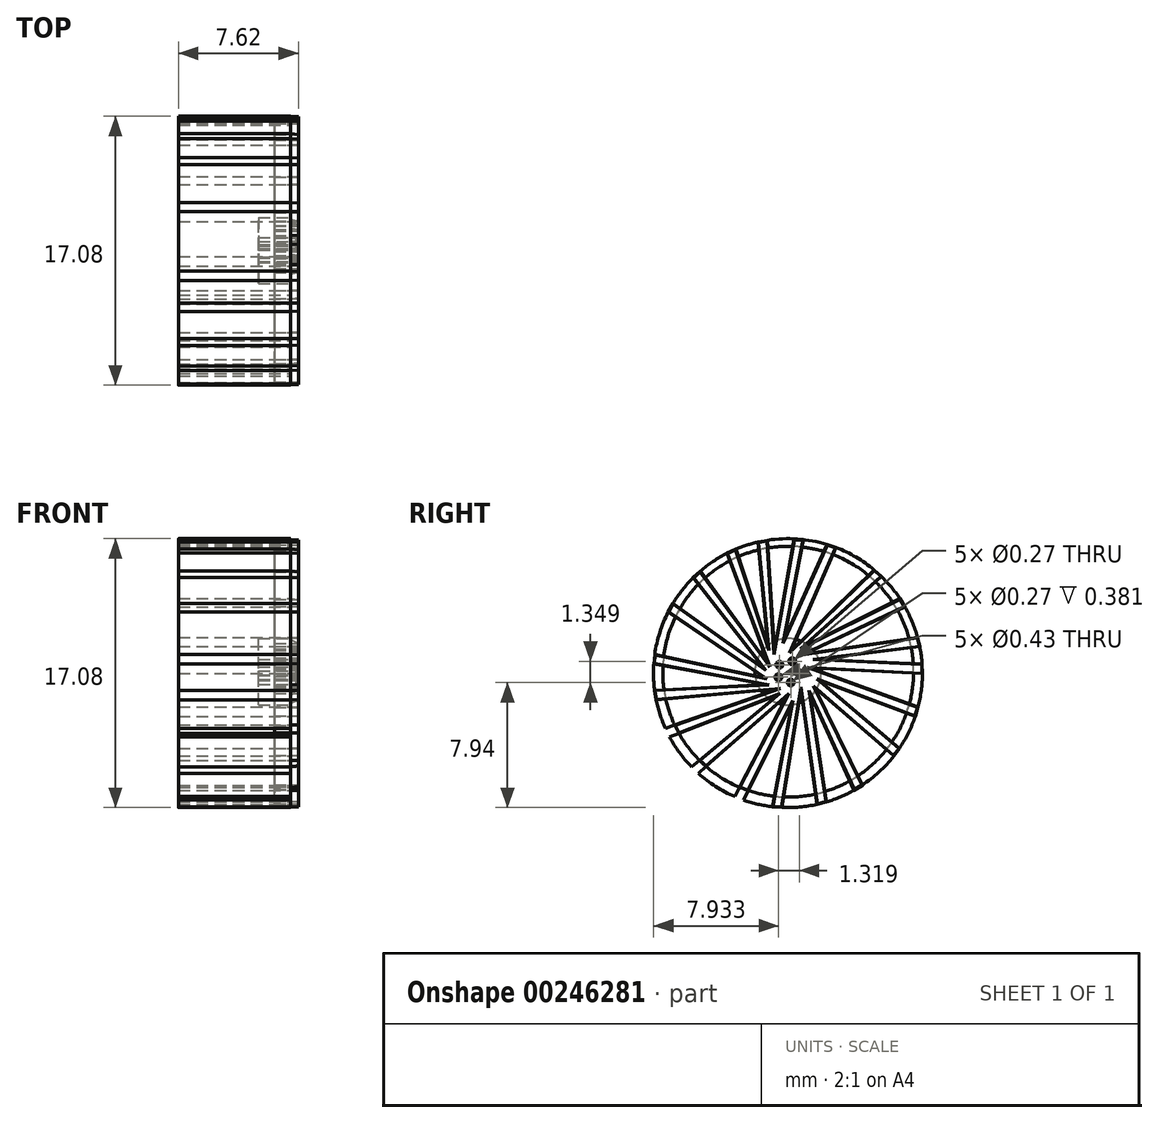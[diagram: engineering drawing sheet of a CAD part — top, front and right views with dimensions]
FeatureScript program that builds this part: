
annotation { "Feature Type Name" : "Feature", "Feature Type Description" : "" }
export const myFeature = defineFeature(function(context is Context, id is Id, definition is map)
    precondition{}
    {
        {
            var Q0;
            Q0=qCreatedBy(makeId("Right.planeOp"),FACE);
            var sketch = newSketch(context, id + "F0", { "sketchPlane" : qUnion([Q0])});
            skCircle(sketch, "E0", {"center": v(-0.01, -0.1) * mm, "radius": 8.54 * mm});
            skCircle(sketch, "E1", {"center": v(0, 0) * mm, "radius": 2.1 * mm});
            skCircle(sketch, "E2", {"center": v(0, 0) * mm, "radius": 7.96 * mm});
            skLineSegment(sketch, "E3", {"start": v(-0.39, -8.62) * mm, "end": v(0.81, -1.16) * mm});
            skLineSegment(sketch, "E4", {"start": v(0.81, -1.16) * mm, "end": v(1.84, -8.43) * mm});
            skLineSegment(sketch, "E5", {"start": v(2.43, -8.27) * mm, "end": v(1.38, -1.38) * mm});
            skLineSegment(sketch, "E6", {"start": v(1.38, -1.38) * mm, "end": v(4.19, -7.53) * mm});
            skLineSegment(sketch, "E7", {"start": v(-1, -8.58) * mm, "end": v(0.24, -2) * mm});
            skLineSegment(sketch, "E8", {"start": v(0.24, -2) * mm, "end": v(-2.83, -8.16) * mm});
            skLineSegment(sketch, "E9", {"start": v(-2.83, -8.16) * mm, "end": v(-3.4, -7.93) * mm});
            skLineSegment(sketch, "E10", {"start": v(-3.4, -7.93) * mm, "end": v(-0.05, -1.48) * mm});
            skLineSegment(sketch, "E11", {"start": v(-0.05, -1.48) * mm, "end": v(-5.7, -6.46) * mm});
            skLineSegment(sketch, "E12", {"start": v(-5.7, -6.46) * mm, "end": v(-6.14, -6.04) * mm});
            skLineSegment(sketch, "E13", {"start": v(-6.14, -6.04) * mm, "end": v(-0.66, -1.47) * mm});
            skLineSegment(sketch, "E14", {"start": v(-0.66, -1.47) * mm, "end": v(-7.53, -4.14) * mm});
            skLineSegment(sketch, "E15", {"start": v(-7.53, -4.14) * mm, "end": v(-7.8, -3.6) * mm});
            skLineSegment(sketch, "E16", {"start": v(-7.8, -3.6) * mm, "end": v(-0.7, -1.1) * mm});
            skLineSegment(sketch, "E17", {"start": v(-0.7, -1.1) * mm, "end": v(-8.39, -1.78) * mm});
            skLineSegment(sketch, "E18", {"start": v(-8.48, -1.18) * mm, "end": v(-1.45, -0.82) * mm});
            skLineSegment(sketch, "E19", {"start": v(-1.45, -0.82) * mm, "end": v(-8.53, 0.5) * mm});
            skLineSegment(sketch, "E20", {"start": v(-8.47, 1.1) * mm, "end": v(-1.46, -0.4) * mm});
            skLineSegment(sketch, "E21", {"start": v(-1.46, -0.4) * mm, "end": v(-7.62, 3.8) * mm});
            skLineSegment(sketch, "E22", {"start": v(-7.32, 4.33) * mm, "end": v(-1.54, 0.2) * mm});
            skLineSegment(sketch, "E23", {"start": v(-1.54, 0.2) * mm, "end": v(-6.03, 5.97) * mm});
            skLineSegment(sketch, "E24", {"start": v(-5.58, 6.38) * mm, "end": v(-1.25, 0.47) * mm});
            skLineSegment(sketch, "E25", {"start": v(4.7, -7.2) * mm, "end": v(1.68, -1) * mm});
            skLineSegment(sketch, "E26", {"start": v(1.68, -1) * mm, "end": v(6.7, -5.36) * mm});
            skLineSegment(sketch, "E27", {"start": v(7.06, -4.87) * mm, "end": v(1.98, -0.54) * mm});
            skLineSegment(sketch, "E28", {"start": v(1.98, -0.54) * mm, "end": v(8.07, -2.83) * mm});
            skLineSegment(sketch, "E29", {"start": v(8.5, 0.48) * mm, "end": v(1.87, 0.78) * mm});
            skLineSegment(sketch, "E30", {"start": v(1.87, 0.78) * mm, "end": v(8.36, 1.6) * mm});
            skLineSegment(sketch, "E31", {"start": v(8.22, 2.19) * mm, "end": v(1.05, 1.12) * mm});
            skLineSegment(sketch, "E32", {"start": v(1.05, 1.12) * mm, "end": v(7.42, 4.12) * mm});
            skLineSegment(sketch, "E33", {"start": v(7.1, 4.64) * mm, "end": v(0.95, 1.57) * mm});
            skLineSegment(sketch, "E34", {"start": v(0.95, 1.57) * mm, "end": v(5.92, 6.05) * mm});
            skLineSegment(sketch, "E35", {"start": v(5.46, 6.46) * mm, "end": v(0.17, 1.3) * mm});
            skLineSegment(sketch, "E36", {"start": v(0.17, 1.3) * mm, "end": v(3.04, 7.88) * mm});
            skLineSegment(sketch, "E37", {"start": v(2.47, 8.08) * mm, "end": v(-0.26, 2.01) * mm});
            skLineSegment(sketch, "E38", {"start": v(-0.26, 2.01) * mm, "end": v(0.99, 8.39) * mm});
            skLineSegment(sketch, "E39", {"start": v(0.38, 8.39) * mm, "end": v(-0.88, 1.31) * mm});
            skLineSegment(sketch, "E40", {"start": v(-0.88, 1.31) * mm, "end": v(-1.3, 8.35) * mm});
            skLineSegment(sketch, "E41", {"start": v(-1.9, 8.24) * mm, "end": v(-1.28, 1.57) * mm});
            skLineSegment(sketch, "E42", {"start": v(-1.28, 1.57) * mm, "end": v(-3.32, 7.78) * mm});
            skLineSegment(sketch, "E43", {"start": v(-3.87, 7.53) * mm, "end": v(-1.25, 0.47) * mm});
            skLineSegment(sketch, "E44", {"start": v(-1.9, 8.24) * mm, "end": v(-1.3, 8.35) * mm});
            skLineSegment(sketch, "E45", {"start": v(0.38, 8.39) * mm, "end": v(0.99, 8.39) * mm});
            skLineSegment(sketch, "E46", {"start": v(2.47, 8.08) * mm, "end": v(3.04, 7.88) * mm});
            skLineSegment(sketch, "E47", {"start": v(-3.32, 7.78) * mm, "end": v(-3.87, 7.53) * mm});
            skLineSegment(sketch, "E48", {"start": v(-5.58, 6.38) * mm, "end": v(-6.03, 5.97) * mm});
            skLineSegment(sketch, "E49", {"start": v(-7.32, 4.33) * mm, "end": v(-7.62, 3.8) * mm});
            skLineSegment(sketch, "E50", {"start": v(-7.8, -3.6) * mm, "end": v(-7.53, -4.14) * mm});
            skLineSegment(sketch, "E51", {"start": v(-6.14, -6.04) * mm, "end": v(-5.7, -6.46) * mm});
            skLineSegment(sketch, "E52", {"start": v(-3.4, -7.93) * mm, "end": v(-2.83, -8.16) * mm});
            skLineSegment(sketch, "E53", {"start": v(-1, -8.58) * mm, "end": v(-0.39, -8.62) * mm});
            skLineSegment(sketch, "E54", {"start": v(1.84, -8.43) * mm, "end": v(2.43, -8.27) * mm});
            skLineSegment(sketch, "E55", {"start": v(4.19, -7.53) * mm, "end": v(4.7, -7.2) * mm});
            skLineSegment(sketch, "E56", {"start": v(6.7, -5.36) * mm, "end": v(7.06, -4.87) * mm});
            skLineSegment(sketch, "E57", {"start": v(8.53, -0.13) * mm, "end": v(8.5, 0.48) * mm});
            skLineSegment(sketch, "E58", {"start": v(8.36, 1.6) * mm, "end": v(8.22, 2.19) * mm});
            skLineSegment(sketch, "E59", {"start": v(7.1, 4.64) * mm, "end": v(7.42, 4.12) * mm});
            skLineSegment(sketch, "E60", {"start": v(5.46, 6.46) * mm, "end": v(5.92, 6.05) * mm});
            skLineSegment(sketch, "E61", {"start": v(-8.47, 1.1) * mm, "end": v(-8.53, 0.5) * mm});
            skLineSegment(sketch, "E62", {"start": v(-8.39, -1.78) * mm, "end": v(-8.48, -1.18) * mm});
            skLineSegment(sketch, "E63", {"start": v(1.4, 0.23) * mm, "end": v(8.25, -2.25) * mm});
            skLineSegment(sketch, "E64", {"start": v(1.4, 0.23) * mm, "end": v(8.53, -0.13) * mm});
            skLineSegment(sketch, "E65", {"start": v(8.25, -2.25) * mm, "end": v(8.07, -2.83) * mm});
            skCircle(sketch, "E66", {"center": v(0, 0) * mm, "radius": 0.52 * mm});
            skCircle(sketch, "E67", {"center": v(0.26, 0.66) * mm, "radius": 0.19 * mm});
            skCircle(sketch, "E68", {"center": v(-0.55, 0.44) * mm, "radius": 0.19 * mm});
            skCircle(sketch, "E69", {"center": v(0.7, -0.1) * mm, "radius": 0.19 * mm});
            skCircle(sketch, "E70", {"center": v(-0.62, -0.35) * mm, "radius": 0.19 * mm});
            skCircle(sketch, "E71", {"center": v(0.16, -0.69) * mm, "radius": 0.19 * mm});
            skCircle(sketch, "E72", {"center": v(0.26, 0.66) * mm, "radius": 0.13 * mm});
            skCircle(sketch, "E73", {"center": v(-0.55, 0.44) * mm, "radius": 0.13 * mm});
            skCircle(sketch, "E74", {"center": v(-0.62, -0.35) * mm, "radius": 0.13 * mm});
            skCircle(sketch, "E75", {"center": v(0.16, -0.69) * mm, "radius": 0.13 * mm});
            skCircle(sketch, "E76", {"center": v(0.7, -0.1) * mm, "radius": 0.13 * mm});
            skLineSegment(sketch, "E77", {"start": v(-2, -1.56) * mm, "end": v(-1.87, -1.94) * mm});
            skLineSegment(sketch, "E78", {"start": v(-1.64, -2.3) * mm, "end": v(-1.36, -2.64) * mm});
            skLineSegment(sketch, "E79", {"start": v(-0.76, -2.86) * mm, "end": v(-0.3, -3.1) * mm});
            skLineSegment(sketch, "E80", {"start": v(0.04, -3.1) * mm, "end": v(0.49, -3.18) * mm});
            skLineSegment(sketch, "E81", {"start": v(1.1, -3.26) * mm, "end": v(1.66, -3.18) * mm});
            skLineSegment(sketch, "E82", {"start": v(2.12, -2.99) * mm, "end": v(2.55, -2.78) * mm});
            skLineSegment(sketch, "E83", {"start": v(3.07, -2.21) * mm, "end": v(3.44, -1.78) * mm});
            skLineSegment(sketch, "E84", {"start": v(3.64, -1.17) * mm, "end": v(3.74, -0.61) * mm});
            skLineSegment(sketch, "E85", {"start": v(-2.23, -1.23) * mm, "end": v(-2.25, -0.86) * mm});
            skLineSegment(sketch, "E86", {"start": v(-2.49, -0.62) * mm, "end": v(-2.4, -0.2) * mm});
            skLineSegment(sketch, "E87", {"start": v(-2.6, 0.38) * mm, "end": v(-2.33, 0.76) * mm});
            skLineSegment(sketch, "E88", {"start": v(-2.26, 1.12) * mm, "end": v(-1.91, 1.37) * mm});
            skLineSegment(sketch, "E89", {"start": v(-1.76, 1.84) * mm, "end": v(-1.4, 1.96) * mm});
            skSolve(sketch);
        }
        {
            var Q0;
            {var subQ36=sQuery(id+"F0.wireOp",EDGE,"E67");Q0=makeQuery(id+"F0.imprint","IMPRINT",FACE,{"disambiguationData":[TD([[makeQuery(id+"F0.imprint","IMPRINT",EDGE,{"derivedFrom":subQ36}),-1.0]])]});}
            var Q1;
            {var subQ0=sQuery(id+"F0.wireOp",EDGE,"E32");var subQ1=sQuery(id+"F0.wireOp",EDGE,"E1");var subQ2=makeQuery(id+"F0.imprint","INTERSECT",VERTEX,{"derivedFrom":[subQ1,subQ0]});Q1=makeQuery(id+"F0.imprint","IMPRINT",FACE,{"disambiguationData":[TD([[makeQuery(id+"F0.imprint","IMPRINT",EDGE,{"disambiguationData":[TD([[subQ2,-1.0]])],"derivedFrom":subQ1}),-1.0]])]});}
            var Q2;
            {var subQ0=sQuery(id+"F0.wireOp",EDGE,"E34");var subQ1=sQuery(id+"F0.wireOp",EDGE,"E1");var subQ2=makeQuery(id+"F0.imprint","INTERSECT",VERTEX,{"derivedFrom":[subQ1,subQ0]});Q2=makeQuery(id+"F0.imprint","IMPRINT",FACE,{"disambiguationData":[TD([[makeQuery(id+"F0.imprint","IMPRINT",EDGE,{"disambiguationData":[TD([[subQ2,-1.0]])],"derivedFrom":subQ1}),-1.0]])]});}
            var Q3;
            {var subQ0=sQuery(id+"F0.wireOp",EDGE,"E36");var subQ1=sQuery(id+"F0.wireOp",EDGE,"E1");var subQ2=makeQuery(id+"F0.imprint","INTERSECT",VERTEX,{"derivedFrom":[subQ1,subQ0]});Q3=makeQuery(id+"F0.imprint","IMPRINT",FACE,{"disambiguationData":[TD([[makeQuery(id+"F0.imprint","IMPRINT",EDGE,{"disambiguationData":[TD([[subQ2,-1.0]])],"derivedFrom":subQ1}),-1.0]])]});}
            var Q4;
            {var subQ0=sQuery(id+"F0.wireOp",EDGE,"E38");var subQ1=sQuery(id+"F0.wireOp",EDGE,"E1");var subQ2=makeQuery(id+"F0.imprint","INTERSECT",VERTEX,{"derivedFrom":[subQ1,subQ0]});Q4=makeQuery(id+"F0.imprint","IMPRINT",FACE,{"disambiguationData":[TD([[makeQuery(id+"F0.imprint","IMPRINT",EDGE,{"disambiguationData":[TD([[subQ2,-1.0]])],"derivedFrom":subQ1}),-1.0]])]});}
            var Q5;
            {var subQ0=sQuery(id+"F0.wireOp",EDGE,"E30");var subQ1=sQuery(id+"F0.wireOp",EDGE,"E1");var subQ2=makeQuery(id+"F0.imprint","INTERSECT",VERTEX,{"derivedFrom":[subQ1,subQ0]});Q5=makeQuery(id+"F0.imprint","IMPRINT",FACE,{"disambiguationData":[TD([[makeQuery(id+"F0.imprint","IMPRINT",EDGE,{"disambiguationData":[TD([[subQ2,-1.0]])],"derivedFrom":subQ1}),-1.0]])]});}
            var Q6;
            {var subQ0=sQuery(id+"F0.wireOp",EDGE,"E29");var subQ1=sQuery(id+"F0.wireOp",EDGE,"E1");var subQ2=makeQuery(id+"F0.imprint","INTERSECT",VERTEX,{"derivedFrom":[subQ1,subQ0]});Q6=makeQuery(id+"F0.imprint","IMPRINT",FACE,{"disambiguationData":[TD([[makeQuery(id+"F0.imprint","IMPRINT",EDGE,{"disambiguationData":[TD([[subQ2,1.0]])],"derivedFrom":subQ1}),-1.0]])]});}
            var Q7;
            {var subQ0=sQuery(id+"F0.wireOp",EDGE,"E28");var subQ1=sQuery(id+"F0.wireOp",EDGE,"E1");var subQ2=makeQuery(id+"F0.imprint","INTERSECT",VERTEX,{"derivedFrom":[subQ1,subQ0]});Q7=makeQuery(id+"F0.imprint","IMPRINT",FACE,{"disambiguationData":[TD([[makeQuery(id+"F0.imprint","IMPRINT",EDGE,{"disambiguationData":[TD([[subQ2,-1.0]])],"derivedFrom":subQ1}),-1.0]])]});}
            var Q8;
            {var subQ0=sQuery(id+"F0.wireOp",EDGE,"E26");var subQ1=sQuery(id+"F0.wireOp",EDGE,"E1");var subQ2=makeQuery(id+"F0.imprint","INTERSECT",VERTEX,{"derivedFrom":[subQ1,subQ0]});Q8=makeQuery(id+"F0.imprint","IMPRINT",FACE,{"disambiguationData":[TD([[makeQuery(id+"F0.imprint","IMPRINT",EDGE,{"disambiguationData":[TD([[subQ2,-1.0]])],"derivedFrom":subQ1}),-1.0]])]});}
            var Q9;
            {var subQ0=sQuery(id+"F0.wireOp",EDGE,"E6");var subQ1=sQuery(id+"F0.wireOp",EDGE,"E1");var subQ2=makeQuery(id+"F0.imprint","INTERSECT",VERTEX,{"derivedFrom":[subQ1,subQ0]});Q9=makeQuery(id+"F0.imprint","IMPRINT",FACE,{"disambiguationData":[TD([[makeQuery(id+"F0.imprint","IMPRINT",EDGE,{"disambiguationData":[TD([[subQ2,-1.0]])],"derivedFrom":subQ1}),-1.0]])]});}
            var Q10;
            {var subQ0=sQuery(id+"F0.wireOp",EDGE,"E4");var subQ1=sQuery(id+"F0.wireOp",EDGE,"E1");var subQ2=makeQuery(id+"F0.imprint","INTERSECT",VERTEX,{"derivedFrom":[subQ1,subQ0]});Q10=makeQuery(id+"F0.imprint","IMPRINT",FACE,{"disambiguationData":[TD([[makeQuery(id+"F0.imprint","IMPRINT",EDGE,{"disambiguationData":[TD([[subQ2,-1.0]])],"derivedFrom":subQ1}),-1.0]])]});}
            var Q11;
            {var subQ0=sQuery(id+"F0.wireOp",EDGE,"E7");var subQ1=sQuery(id+"F0.wireOp",EDGE,"E1");var subQ2=makeQuery(id+"F0.imprint","INTERSECT",VERTEX,{"derivedFrom":[subQ1,subQ0]});Q11=makeQuery(id+"F0.imprint","IMPRINT",FACE,{"disambiguationData":[TD([[makeQuery(id+"F0.imprint","IMPRINT",EDGE,{"disambiguationData":[TD([[subQ2,-1.0]])],"derivedFrom":subQ1}),-1.0]])]});}
            var Q12;
            {var subQ0=sQuery(id+"F0.wireOp",EDGE,"E10");var subQ1=sQuery(id+"F0.wireOp",EDGE,"E1");var subQ2=makeQuery(id+"F0.imprint","INTERSECT",VERTEX,{"derivedFrom":[subQ1,subQ0]});Q12=makeQuery(id+"F0.imprint","IMPRINT",FACE,{"disambiguationData":[TD([[makeQuery(id+"F0.imprint","IMPRINT",EDGE,{"disambiguationData":[TD([[subQ2,-1.0]])],"derivedFrom":subQ1}),-1.0]])]});}
            var Q13;
            {var subQ0=sQuery(id+"F0.wireOp",EDGE,"E13");var subQ1=sQuery(id+"F0.wireOp",EDGE,"E1");var subQ2=makeQuery(id+"F0.imprint","INTERSECT",VERTEX,{"derivedFrom":[subQ1,subQ0]});Q13=makeQuery(id+"F0.imprint","IMPRINT",FACE,{"disambiguationData":[TD([[makeQuery(id+"F0.imprint","IMPRINT",EDGE,{"disambiguationData":[TD([[subQ2,-1.0]])],"derivedFrom":subQ1}),-1.0]])]});}
            var Q14;
            {var subQ0=sQuery(id+"F0.wireOp",EDGE,"E16");var subQ1=sQuery(id+"F0.wireOp",EDGE,"E1");var subQ2=makeQuery(id+"F0.imprint","INTERSECT",VERTEX,{"derivedFrom":[subQ1,subQ0]});Q14=makeQuery(id+"F0.imprint","IMPRINT",FACE,{"disambiguationData":[TD([[makeQuery(id+"F0.imprint","IMPRINT",EDGE,{"disambiguationData":[TD([[subQ2,-1.0]])],"derivedFrom":subQ1}),-1.0]])]});}
            var Q15;
            {var subQ0=sQuery(id+"F0.wireOp",EDGE,"E18");var subQ1=sQuery(id+"F0.wireOp",EDGE,"E1");var subQ2=makeQuery(id+"F0.imprint","INTERSECT",VERTEX,{"derivedFrom":[subQ1,subQ0]});Q15=makeQuery(id+"F0.imprint","IMPRINT",FACE,{"disambiguationData":[TD([[makeQuery(id+"F0.imprint","IMPRINT",EDGE,{"disambiguationData":[TD([[subQ2,-1.0]])],"derivedFrom":subQ1}),-1.0]])]});}
            var Q16;
            {var subQ0=sQuery(id+"F0.wireOp",EDGE,"E20");var subQ1=sQuery(id+"F0.wireOp",EDGE,"E1");var subQ2=makeQuery(id+"F0.imprint","INTERSECT",VERTEX,{"derivedFrom":[subQ1,subQ0]});Q16=makeQuery(id+"F0.imprint","IMPRINT",FACE,{"disambiguationData":[TD([[makeQuery(id+"F0.imprint","IMPRINT",EDGE,{"disambiguationData":[TD([[subQ2,-1.0]])],"derivedFrom":subQ1}),-1.0]])]});}
            var Q17;
            {var subQ0=sQuery(id+"F0.wireOp",EDGE,"E22");var subQ1=sQuery(id+"F0.wireOp",EDGE,"E1");var subQ2=makeQuery(id+"F0.imprint","INTERSECT",VERTEX,{"derivedFrom":[subQ1,subQ0]});Q17=makeQuery(id+"F0.imprint","IMPRINT",FACE,{"disambiguationData":[TD([[makeQuery(id+"F0.imprint","IMPRINT",EDGE,{"disambiguationData":[TD([[subQ2,-1.0]])],"derivedFrom":subQ1}),-1.0]])]});}
            var Q18;
            {var subQ0=sQuery(id+"F0.wireOp",EDGE,"E24");var subQ1=sQuery(id+"F0.wireOp",EDGE,"E1");var subQ2=makeQuery(id+"F0.imprint","INTERSECT",VERTEX,{"derivedFrom":[subQ1,subQ0]});Q18=makeQuery(id+"F0.imprint","IMPRINT",FACE,{"disambiguationData":[TD([[makeQuery(id+"F0.imprint","IMPRINT",EDGE,{"disambiguationData":[TD([[subQ2,-1.0]])],"derivedFrom":subQ1}),-1.0]])]});}
            var Q19;
            {var subQ0=sQuery(id+"F0.wireOp",EDGE,"E42");var subQ1=sQuery(id+"F0.wireOp",EDGE,"E1");var subQ2=makeQuery(id+"F0.imprint","INTERSECT",VERTEX,{"derivedFrom":[subQ1,subQ0]});Q19=makeQuery(id+"F0.imprint","IMPRINT",FACE,{"disambiguationData":[TD([[makeQuery(id+"F0.imprint","IMPRINT",EDGE,{"disambiguationData":[TD([[subQ2,-1.0]])],"derivedFrom":subQ1}),-1.0]])]});}
            var Q20;
            {var subQ0=sQuery(id+"F0.wireOp",EDGE,"E40");var subQ1=sQuery(id+"F0.wireOp",EDGE,"E1");var subQ2=makeQuery(id+"F0.imprint","INTERSECT",VERTEX,{"derivedFrom":[subQ1,subQ0]});Q20=makeQuery(id+"F0.imprint","IMPRINT",FACE,{"disambiguationData":[TD([[makeQuery(id+"F0.imprint","IMPRINT",EDGE,{"disambiguationData":[TD([[subQ2,-1.0]])],"derivedFrom":subQ1}),-1.0]])]});}
            var Q21;
            {var subQ5=sQuery(id+"F0.wireOp",EDGE,"E57");Q21=makeQuery(id+"F0.imprint","IMPRINT",FACE,{"disambiguationData":[TD([[makeQuery(id+"F0.imprint","IMPRINT",EDGE,{"derivedFrom":subQ5}),1.0]])]});}
            var Q22;
            {var subQ5=sQuery(id+"F0.wireOp",EDGE,"E58");Q22=makeQuery(id+"F0.imprint","IMPRINT",FACE,{"disambiguationData":[TD([[makeQuery(id+"F0.imprint","IMPRINT",EDGE,{"derivedFrom":subQ5}),1.0]])]});}
            var Q23;
            {var subQ5=sQuery(id+"F0.wireOp",EDGE,"E59");Q23=makeQuery(id+"F0.imprint","IMPRINT",FACE,{"disambiguationData":[TD([[makeQuery(id+"F0.imprint","IMPRINT",EDGE,{"derivedFrom":subQ5}),-1.0]])]});}
            var Q24;
            {var subQ5=sQuery(id+"F0.wireOp",EDGE,"E60");Q24=makeQuery(id+"F0.imprint","IMPRINT",FACE,{"disambiguationData":[TD([[makeQuery(id+"F0.imprint","IMPRINT",EDGE,{"derivedFrom":subQ5}),-1.0]])]});}
            var Q25;
            {var subQ5=sQuery(id+"F0.wireOp",EDGE,"E46");Q25=makeQuery(id+"F0.imprint","IMPRINT",FACE,{"disambiguationData":[TD([[makeQuery(id+"F0.imprint","IMPRINT",EDGE,{"derivedFrom":subQ5}),-1.0]])]});}
            var Q26;
            {var subQ5=sQuery(id+"F0.wireOp",EDGE,"E45");Q26=makeQuery(id+"F0.imprint","IMPRINT",FACE,{"disambiguationData":[TD([[makeQuery(id+"F0.imprint","IMPRINT",EDGE,{"derivedFrom":subQ5}),-1.0]])]});}
            var Q27;
            {var subQ5=sQuery(id+"F0.wireOp",EDGE,"E44");Q27=makeQuery(id+"F0.imprint","IMPRINT",FACE,{"disambiguationData":[TD([[makeQuery(id+"F0.imprint","IMPRINT",EDGE,{"derivedFrom":subQ5}),-1.0]])]});}
            var Q28;
            {var subQ5=sQuery(id+"F0.wireOp",EDGE,"E47");Q28=makeQuery(id+"F0.imprint","IMPRINT",FACE,{"disambiguationData":[TD([[makeQuery(id+"F0.imprint","IMPRINT",EDGE,{"derivedFrom":subQ5}),1.0]])]});}
            var Q29;
            {var subQ5=sQuery(id+"F0.wireOp",EDGE,"E48");Q29=makeQuery(id+"F0.imprint","IMPRINT",FACE,{"disambiguationData":[TD([[makeQuery(id+"F0.imprint","IMPRINT",EDGE,{"derivedFrom":subQ5}),1.0]])]});}
            var Q30;
            {var subQ5=sQuery(id+"F0.wireOp",EDGE,"E49");Q30=makeQuery(id+"F0.imprint","IMPRINT",FACE,{"disambiguationData":[TD([[makeQuery(id+"F0.imprint","IMPRINT",EDGE,{"derivedFrom":subQ5}),1.0]])]});}
            var Q31;
            {var subQ5=sQuery(id+"F0.wireOp",EDGE,"E61");Q31=makeQuery(id+"F0.imprint","IMPRINT",FACE,{"disambiguationData":[TD([[makeQuery(id+"F0.imprint","IMPRINT",EDGE,{"derivedFrom":subQ5}),1.0]])]});}
            var Q32;
            {var subQ5=sQuery(id+"F0.wireOp",EDGE,"E62");Q32=makeQuery(id+"F0.imprint","IMPRINT",FACE,{"disambiguationData":[TD([[makeQuery(id+"F0.imprint","IMPRINT",EDGE,{"derivedFrom":subQ5}),-1.0]])]});}
            var Q33;
            {var subQ5=sQuery(id+"F0.wireOp",EDGE,"E50");Q33=makeQuery(id+"F0.imprint","IMPRINT",FACE,{"disambiguationData":[TD([[makeQuery(id+"F0.imprint","IMPRINT",EDGE,{"derivedFrom":subQ5}),1.0]])]});}
            var Q34;
            {var subQ5=sQuery(id+"F0.wireOp",EDGE,"E51");Q34=makeQuery(id+"F0.imprint","IMPRINT",FACE,{"disambiguationData":[TD([[makeQuery(id+"F0.imprint","IMPRINT",EDGE,{"derivedFrom":subQ5}),1.0]])]});}
            var Q35;
            {var subQ5=sQuery(id+"F0.wireOp",EDGE,"E52");Q35=makeQuery(id+"F0.imprint","IMPRINT",FACE,{"disambiguationData":[TD([[makeQuery(id+"F0.imprint","IMPRINT",EDGE,{"derivedFrom":subQ5}),1.0]])]});}
            var Q36;
            {var subQ5=sQuery(id+"F0.wireOp",EDGE,"E53");Q36=makeQuery(id+"F0.imprint","IMPRINT",FACE,{"disambiguationData":[TD([[makeQuery(id+"F0.imprint","IMPRINT",EDGE,{"derivedFrom":subQ5}),1.0]])]});}
            var Q37;
            {var subQ5=sQuery(id+"F0.wireOp",EDGE,"E54");Q37=makeQuery(id+"F0.imprint","IMPRINT",FACE,{"disambiguationData":[TD([[makeQuery(id+"F0.imprint","IMPRINT",EDGE,{"derivedFrom":subQ5}),1.0]])]});}
            var Q38;
            {var subQ5=sQuery(id+"F0.wireOp",EDGE,"E55");Q38=makeQuery(id+"F0.imprint","IMPRINT",FACE,{"disambiguationData":[TD([[makeQuery(id+"F0.imprint","IMPRINT",EDGE,{"derivedFrom":subQ5}),1.0]])]});}
            var Q39;
            {var subQ5=sQuery(id+"F0.wireOp",EDGE,"E56");Q39=makeQuery(id+"F0.imprint","IMPRINT",FACE,{"disambiguationData":[TD([[makeQuery(id+"F0.imprint","IMPRINT",EDGE,{"derivedFrom":subQ5}),1.0]])]});}
            var Q40;
            {var subQ5=sQuery(id+"F0.wireOp",EDGE,"E65");Q40=makeQuery(id+"F0.imprint","IMPRINT",FACE,{"disambiguationData":[TD([[makeQuery(id+"F0.imprint","IMPRINT",EDGE,{"derivedFrom":subQ5}),-1.0]])]});}
            var Q41;
            {var subQ0=sQuery(id+"F0.wireOp",EDGE,"E66");var subQ4=makeQuery(id+"F0.imprint","INTERSECT",VERTEX,{"derivedFrom":[subQ0,sQuery(id+"F0.wireOp",EDGE,"E68")]});Q41=makeQuery(id+"F0.imprint","IMPRINT",FACE,{"disambiguationData":[TD([[makeQuery(id+"F0.imprint","IMPRINT",EDGE,{"disambiguationData":[TD([[subQ4,1.0]])],"derivedFrom":subQ0}),1.0]])]});}
            var Q42;
            {var subQ5=sQuery(id+"F0.wireOp",EDGE,"E84");Q42=makeQuery(id+"F0.imprint","IMPRINT",FACE,{"disambiguationData":[TD([[makeQuery(id+"F0.imprint","IMPRINT",EDGE,{"derivedFrom":subQ5}),-1.0]])]});}
            var Q43;
            {var subQ5=sQuery(id+"F0.wireOp",EDGE,"E83");Q43=makeQuery(id+"F0.imprint","IMPRINT",FACE,{"disambiguationData":[TD([[makeQuery(id+"F0.imprint","IMPRINT",EDGE,{"derivedFrom":subQ5}),-1.0]])]});}
            var Q44;
            {var subQ5=sQuery(id+"F0.wireOp",EDGE,"E82");Q44=makeQuery(id+"F0.imprint","IMPRINT",FACE,{"disambiguationData":[TD([[makeQuery(id+"F0.imprint","IMPRINT",EDGE,{"derivedFrom":subQ5}),-1.0]])]});}
            var Q45;
            {var subQ5=sQuery(id+"F0.wireOp",EDGE,"E81");Q45=makeQuery(id+"F0.imprint","IMPRINT",FACE,{"disambiguationData":[TD([[makeQuery(id+"F0.imprint","IMPRINT",EDGE,{"derivedFrom":subQ5}),-1.0]])]});}
            var Q46;
            {var subQ5=sQuery(id+"F0.wireOp",EDGE,"E80");Q46=makeQuery(id+"F0.imprint","IMPRINT",FACE,{"disambiguationData":[TD([[makeQuery(id+"F0.imprint","IMPRINT",EDGE,{"derivedFrom":subQ5}),-1.0]])]});}
            var Q47;
            {var subQ5=sQuery(id+"F0.wireOp",EDGE,"E79");Q47=makeQuery(id+"F0.imprint","IMPRINT",FACE,{"disambiguationData":[TD([[makeQuery(id+"F0.imprint","IMPRINT",EDGE,{"derivedFrom":subQ5}),-1.0]])]});}
            var Q48;
            {var subQ5=sQuery(id+"F0.wireOp",EDGE,"E78");Q48=makeQuery(id+"F0.imprint","IMPRINT",FACE,{"disambiguationData":[TD([[makeQuery(id+"F0.imprint","IMPRINT",EDGE,{"derivedFrom":subQ5}),-1.0]])]});}
            var Q49;
            {var subQ5=sQuery(id+"F0.wireOp",EDGE,"E77");Q49=makeQuery(id+"F0.imprint","IMPRINT",FACE,{"disambiguationData":[TD([[makeQuery(id+"F0.imprint","IMPRINT",EDGE,{"derivedFrom":subQ5}),-1.0]])]});}
            var Q50;
            {var subQ5=sQuery(id+"F0.wireOp",EDGE,"E85");Q50=makeQuery(id+"F0.imprint","IMPRINT",FACE,{"disambiguationData":[TD([[makeQuery(id+"F0.imprint","IMPRINT",EDGE,{"derivedFrom":subQ5}),1.0]])]});}
            var Q51;
            {var subQ5=sQuery(id+"F0.wireOp",EDGE,"E87");Q51=makeQuery(id+"F0.imprint","IMPRINT",FACE,{"disambiguationData":[TD([[makeQuery(id+"F0.imprint","IMPRINT",EDGE,{"derivedFrom":subQ5}),1.0]])]});}
            var Q52;
            {var subQ5=sQuery(id+"F0.wireOp",EDGE,"E88");Q52=makeQuery(id+"F0.imprint","IMPRINT",FACE,{"disambiguationData":[TD([[makeQuery(id+"F0.imprint","IMPRINT",EDGE,{"derivedFrom":subQ5}),1.0]])]});}
            var Q53;
            {var subQ5=sQuery(id+"F0.wireOp",EDGE,"E89");Q53=makeQuery(id+"F0.imprint","IMPRINT",FACE,{"disambiguationData":[TD([[makeQuery(id+"F0.imprint","IMPRINT",EDGE,{"derivedFrom":subQ5}),1.0]])]});}
            extrude(context, id + "F1", {"entities" : qUnion([Q0, Q1, Q2, Q3, Q4, Q5, Q6, Q7, Q8, Q9, Q10, Q11, Q12, Q13, Q14, Q15, Q16, Q17, Q18, Q19, Q20, Q21, Q22, Q23, Q24, Q25, Q26, Q27, Q28, Q29, Q30, Q31, Q32, Q33, Q34, Q35, Q36, Q37, Q38, Q39, Q40, Q41, Q42, Q43, Q44, Q45, Q46, Q47, Q48, Q49, Q50, Q51, Q52, Q53]), "depth" : 0.5 * mm, "hasDraft" : true, "draftAngle" : 3 * degree, "draftPullDirection" : true});
        }
        {
            var Q0;
            Q0=makeQuery(id+"F0.imprint","IMPRINT",FACE,{"disambiguationData":[TD([[makeQuery(id+"F0.imprint","IMPRINT",EDGE,{"derivedFrom":sQuery(id+"F0.wireOp",EDGE,"E67")}),1.0]])]});
            var Q1;
            Q1=makeQuery(id+"F0.imprint","IMPRINT",FACE,{"disambiguationData":[TD([[makeQuery(id+"F0.imprint","IMPRINT",EDGE,{"derivedFrom":sQuery(id+"F0.wireOp",EDGE,"E68")}),1.0]])]});
            var Q2;
            Q2=makeQuery(id+"F0.imprint","IMPRINT",FACE,{"disambiguationData":[TD([[makeQuery(id+"F0.imprint","IMPRINT",EDGE,{"derivedFrom":sQuery(id+"F0.wireOp",EDGE,"E69")}),1.0]])]});
            var Q3;
            Q3=makeQuery(id+"F0.imprint","IMPRINT",FACE,{"disambiguationData":[TD([[makeQuery(id+"F0.imprint","IMPRINT",EDGE,{"derivedFrom":sQuery(id+"F0.wireOp",EDGE,"E71")}),1.0]])]});
            var Q4;
            Q4=makeQuery(id+"F0.imprint","IMPRINT",FACE,{"disambiguationData":[TD([[makeQuery(id+"F0.imprint","IMPRINT",EDGE,{"derivedFrom":sQuery(id+"F0.wireOp",EDGE,"E70")}),1.0]])]});
            extrude(context, id + "F2", {"entities" : qUnion([Q0, Q1, Q2, Q3, Q4]), "depth" : 0.38 * mm});
        }
        {
            var Q0;
            {var subQ3=sQuery(id+"F0.wireOp",EDGE,"E43");var subQ5=sQuery(id+"F0.wireOp",EDGE,"E2");var subQ6=makeQuery(id+"F0.imprint","INTERSECT",VERTEX,{"derivedFrom":[subQ5,subQ3]});Q0=makeQuery(id+"F0.imprint","IMPRINT",FACE,{"disambiguationData":[TD([[makeQuery(id+"F0.imprint","IMPRINT",EDGE,{"disambiguationData":[TD([[subQ6,-1.0]])],"derivedFrom":subQ5}),-1.0]])]});}
            var Q1;
            {var subQ5=sQuery(id+"F0.wireOp",EDGE,"E48");Q1=makeQuery(id+"F0.imprint","IMPRINT",FACE,{"disambiguationData":[TD([[makeQuery(id+"F0.imprint","IMPRINT",EDGE,{"derivedFrom":subQ5}),1.0]])]});}
            var Q2;
            {var subQ3=sQuery(id+"F0.wireOp",EDGE,"E23");var subQ5=sQuery(id+"F0.wireOp",EDGE,"E2");var subQ7=makeQuery(id+"F0.imprint","INTERSECT",VERTEX,{"derivedFrom":[subQ5,subQ3]});Q2=makeQuery(id+"F0.imprint","IMPRINT",FACE,{"disambiguationData":[TD([[makeQuery(id+"F0.imprint","IMPRINT",EDGE,{"disambiguationData":[TD([[subQ7,-1.0]])],"derivedFrom":subQ5}),-1.0]])]});}
            var Q3;
            {var subQ5=sQuery(id+"F0.wireOp",EDGE,"E49");Q3=makeQuery(id+"F0.imprint","IMPRINT",FACE,{"disambiguationData":[TD([[makeQuery(id+"F0.imprint","IMPRINT",EDGE,{"derivedFrom":subQ5}),1.0]])]});}
            var Q4;
            {var subQ3=sQuery(id+"F0.wireOp",EDGE,"E21");var subQ5=sQuery(id+"F0.wireOp",EDGE,"E2");var subQ7=makeQuery(id+"F0.imprint","INTERSECT",VERTEX,{"derivedFrom":[subQ5,subQ3]});Q4=makeQuery(id+"F0.imprint","IMPRINT",FACE,{"disambiguationData":[TD([[makeQuery(id+"F0.imprint","IMPRINT",EDGE,{"disambiguationData":[TD([[subQ7,-1.0]])],"derivedFrom":subQ5}),-1.0]])]});}
            var Q5;
            {var subQ5=sQuery(id+"F0.wireOp",EDGE,"E61");Q5=makeQuery(id+"F0.imprint","IMPRINT",FACE,{"disambiguationData":[TD([[makeQuery(id+"F0.imprint","IMPRINT",EDGE,{"derivedFrom":subQ5}),1.0]])]});}
            var Q6;
            {var subQ3=sQuery(id+"F0.wireOp",EDGE,"E19");var subQ5=sQuery(id+"F0.wireOp",EDGE,"E2");var subQ6=makeQuery(id+"F0.imprint","INTERSECT",VERTEX,{"derivedFrom":[subQ5,subQ3]});Q6=makeQuery(id+"F0.imprint","IMPRINT",FACE,{"disambiguationData":[TD([[makeQuery(id+"F0.imprint","IMPRINT",EDGE,{"disambiguationData":[TD([[subQ6,-1.0]])],"derivedFrom":subQ5}),-1.0]])]});}
            var Q7;
            {var subQ5=sQuery(id+"F0.wireOp",EDGE,"E62");Q7=makeQuery(id+"F0.imprint","IMPRINT",FACE,{"disambiguationData":[TD([[makeQuery(id+"F0.imprint","IMPRINT",EDGE,{"derivedFrom":subQ5}),-1.0]])]});}
            var Q8;
            {var subQ3=sQuery(id+"F0.wireOp",EDGE,"E17");var subQ5=sQuery(id+"F0.wireOp",EDGE,"E2");var subQ7=makeQuery(id+"F0.imprint","INTERSECT",VERTEX,{"derivedFrom":[subQ5,subQ3]});Q8=makeQuery(id+"F0.imprint","IMPRINT",FACE,{"disambiguationData":[TD([[makeQuery(id+"F0.imprint","IMPRINT",EDGE,{"disambiguationData":[TD([[subQ7,-1.0]])],"derivedFrom":subQ5}),-1.0]])]});}
            var Q9;
            {var subQ5=sQuery(id+"F0.wireOp",EDGE,"E50");Q9=makeQuery(id+"F0.imprint","IMPRINT",FACE,{"disambiguationData":[TD([[makeQuery(id+"F0.imprint","IMPRINT",EDGE,{"derivedFrom":subQ5}),1.0]])]});}
            var Q10;
            {var subQ3=sQuery(id+"F0.wireOp",EDGE,"E14");var subQ5=sQuery(id+"F0.wireOp",EDGE,"E2");var subQ6=makeQuery(id+"F0.imprint","INTERSECT",VERTEX,{"derivedFrom":[subQ5,subQ3]});Q10=makeQuery(id+"F0.imprint","IMPRINT",FACE,{"disambiguationData":[TD([[makeQuery(id+"F0.imprint","IMPRINT",EDGE,{"disambiguationData":[TD([[subQ6,-1.0]])],"derivedFrom":subQ5}),-1.0]])]});}
            var Q11;
            {var subQ5=sQuery(id+"F0.wireOp",EDGE,"E51");Q11=makeQuery(id+"F0.imprint","IMPRINT",FACE,{"disambiguationData":[TD([[makeQuery(id+"F0.imprint","IMPRINT",EDGE,{"derivedFrom":subQ5}),1.0]])]});}
            var Q12;
            {var subQ3=sQuery(id+"F0.wireOp",EDGE,"E11");var subQ5=sQuery(id+"F0.wireOp",EDGE,"E2");var subQ6=makeQuery(id+"F0.imprint","INTERSECT",VERTEX,{"derivedFrom":[subQ5,subQ3]});Q12=makeQuery(id+"F0.imprint","IMPRINT",FACE,{"disambiguationData":[TD([[makeQuery(id+"F0.imprint","IMPRINT",EDGE,{"disambiguationData":[TD([[subQ6,-1.0]])],"derivedFrom":subQ5}),-1.0]])]});}
            var Q13;
            {var subQ5=sQuery(id+"F0.wireOp",EDGE,"E52");Q13=makeQuery(id+"F0.imprint","IMPRINT",FACE,{"disambiguationData":[TD([[makeQuery(id+"F0.imprint","IMPRINT",EDGE,{"derivedFrom":subQ5}),1.0]])]});}
            var Q14;
            {var subQ3=sQuery(id+"F0.wireOp",EDGE,"E8");var subQ5=sQuery(id+"F0.wireOp",EDGE,"E2");var subQ6=makeQuery(id+"F0.imprint","INTERSECT",VERTEX,{"derivedFrom":[subQ5,subQ3]});Q14=makeQuery(id+"F0.imprint","IMPRINT",FACE,{"disambiguationData":[TD([[makeQuery(id+"F0.imprint","IMPRINT",EDGE,{"disambiguationData":[TD([[subQ6,-1.0]])],"derivedFrom":subQ5}),-1.0]])]});}
            var Q15;
            {var subQ5=sQuery(id+"F0.wireOp",EDGE,"E47");Q15=makeQuery(id+"F0.imprint","IMPRINT",FACE,{"disambiguationData":[TD([[makeQuery(id+"F0.imprint","IMPRINT",EDGE,{"derivedFrom":subQ5}),1.0]])]});}
            var Q16;
            {var subQ0=sQuery(id+"F0.wireOp",EDGE,"E41");var subQ5=sQuery(id+"F0.wireOp",EDGE,"E2");var subQ6=makeQuery(id+"F0.imprint","INTERSECT",VERTEX,{"derivedFrom":[subQ5,subQ0]});Q16=makeQuery(id+"F0.imprint","IMPRINT",FACE,{"disambiguationData":[TD([[makeQuery(id+"F0.imprint","IMPRINT",EDGE,{"disambiguationData":[TD([[subQ6,-1.0]])],"derivedFrom":subQ5}),-1.0]])]});}
            var Q17;
            {var subQ5=sQuery(id+"F0.wireOp",EDGE,"E44");Q17=makeQuery(id+"F0.imprint","IMPRINT",FACE,{"disambiguationData":[TD([[makeQuery(id+"F0.imprint","IMPRINT",EDGE,{"derivedFrom":subQ5}),-1.0]])]});}
            var Q18;
            {var subQ7=sQuery(id+"F0.wireOp",EDGE,"E45");Q18=makeQuery(id+"F0.imprint","IMPRINT",FACE,{"disambiguationData":[TD([[makeQuery(id+"F0.imprint","IMPRINT",EDGE,{"derivedFrom":subQ7}),1.0]])]});}
            var Q19;
            {var subQ5=sQuery(id+"F0.wireOp",EDGE,"E45");Q19=makeQuery(id+"F0.imprint","IMPRINT",FACE,{"disambiguationData":[TD([[makeQuery(id+"F0.imprint","IMPRINT",EDGE,{"derivedFrom":subQ5}),-1.0]])]});}
            var Q20;
            {var subQ0=sQuery(id+"F0.wireOp",EDGE,"E37");var subQ5=sQuery(id+"F0.wireOp",EDGE,"E2");var subQ7=makeQuery(id+"F0.imprint","INTERSECT",VERTEX,{"derivedFrom":[subQ5,subQ0]});Q20=makeQuery(id+"F0.imprint","IMPRINT",FACE,{"disambiguationData":[TD([[makeQuery(id+"F0.imprint","IMPRINT",EDGE,{"disambiguationData":[TD([[subQ7,-1.0]])],"derivedFrom":subQ5}),-1.0]])]});}
            var Q21;
            {var subQ5=sQuery(id+"F0.wireOp",EDGE,"E46");Q21=makeQuery(id+"F0.imprint","IMPRINT",FACE,{"disambiguationData":[TD([[makeQuery(id+"F0.imprint","IMPRINT",EDGE,{"derivedFrom":subQ5}),-1.0]])]});}
            var Q22;
            {var subQ0=sQuery(id+"F0.wireOp",EDGE,"E35");var subQ5=sQuery(id+"F0.wireOp",EDGE,"E2");var subQ6=makeQuery(id+"F0.imprint","INTERSECT",VERTEX,{"derivedFrom":[subQ5,subQ0]});Q22=makeQuery(id+"F0.imprint","IMPRINT",FACE,{"disambiguationData":[TD([[makeQuery(id+"F0.imprint","IMPRINT",EDGE,{"disambiguationData":[TD([[subQ6,-1.0]])],"derivedFrom":subQ5}),-1.0]])]});}
            var Q23;
            {var subQ5=sQuery(id+"F0.wireOp",EDGE,"E60");Q23=makeQuery(id+"F0.imprint","IMPRINT",FACE,{"disambiguationData":[TD([[makeQuery(id+"F0.imprint","IMPRINT",EDGE,{"derivedFrom":subQ5}),-1.0]])]});}
            var Q24;
            {var subQ0=sQuery(id+"F0.wireOp",EDGE,"E33");var subQ5=sQuery(id+"F0.wireOp",EDGE,"E2");var subQ6=makeQuery(id+"F0.imprint","INTERSECT",VERTEX,{"derivedFrom":[subQ5,subQ0]});Q24=makeQuery(id+"F0.imprint","IMPRINT",FACE,{"disambiguationData":[TD([[makeQuery(id+"F0.imprint","IMPRINT",EDGE,{"disambiguationData":[TD([[subQ6,-1.0]])],"derivedFrom":subQ5}),-1.0]])]});}
            var Q25;
            {var subQ5=sQuery(id+"F0.wireOp",EDGE,"E59");Q25=makeQuery(id+"F0.imprint","IMPRINT",FACE,{"disambiguationData":[TD([[makeQuery(id+"F0.imprint","IMPRINT",EDGE,{"derivedFrom":subQ5}),-1.0]])]});}
            var Q26;
            {var subQ0=sQuery(id+"F0.wireOp",EDGE,"E31");var subQ5=sQuery(id+"F0.wireOp",EDGE,"E2");var subQ6=makeQuery(id+"F0.imprint","INTERSECT",VERTEX,{"derivedFrom":[subQ5,subQ0]});Q26=makeQuery(id+"F0.imprint","IMPRINT",FACE,{"disambiguationData":[TD([[makeQuery(id+"F0.imprint","IMPRINT",EDGE,{"disambiguationData":[TD([[subQ6,-1.0]])],"derivedFrom":subQ5}),-1.0]])]});}
            var Q27;
            {var subQ5=sQuery(id+"F0.wireOp",EDGE,"E58");Q27=makeQuery(id+"F0.imprint","IMPRINT",FACE,{"disambiguationData":[TD([[makeQuery(id+"F0.imprint","IMPRINT",EDGE,{"derivedFrom":subQ5}),1.0]])]});}
            var Q28;
            {var subQ3=sQuery(id+"F0.wireOp",EDGE,"E30");var subQ5=sQuery(id+"F0.wireOp",EDGE,"E2");var subQ6=makeQuery(id+"F0.imprint","INTERSECT",VERTEX,{"derivedFrom":[subQ5,subQ3]});Q28=makeQuery(id+"F0.imprint","IMPRINT",FACE,{"disambiguationData":[TD([[makeQuery(id+"F0.imprint","IMPRINT",EDGE,{"disambiguationData":[TD([[subQ6,1.0]])],"derivedFrom":subQ5}),-1.0]])]});}
            var Q29;
            {var subQ5=sQuery(id+"F0.wireOp",EDGE,"E57");Q29=makeQuery(id+"F0.imprint","IMPRINT",FACE,{"disambiguationData":[TD([[makeQuery(id+"F0.imprint","IMPRINT",EDGE,{"derivedFrom":subQ5}),1.0]])]});}
            var Q30;
            {var subQ3=sQuery(id+"F0.wireOp",EDGE,"E63");var subQ5=sQuery(id+"F0.wireOp",EDGE,"E2");var subQ6=makeQuery(id+"F0.imprint","INTERSECT",VERTEX,{"derivedFrom":[subQ5,subQ3]});Q30=makeQuery(id+"F0.imprint","IMPRINT",FACE,{"disambiguationData":[TD([[makeQuery(id+"F0.imprint","IMPRINT",EDGE,{"disambiguationData":[TD([[subQ6,-1.0]])],"derivedFrom":subQ5}),-1.0]])]});}
            var Q31;
            {var subQ5=sQuery(id+"F0.wireOp",EDGE,"E65");Q31=makeQuery(id+"F0.imprint","IMPRINT",FACE,{"disambiguationData":[TD([[makeQuery(id+"F0.imprint","IMPRINT",EDGE,{"derivedFrom":subQ5}),-1.0]])]});}
            var Q32;
            {var subQ0=sQuery(id+"F0.wireOp",EDGE,"E27");var subQ5=sQuery(id+"F0.wireOp",EDGE,"E2");var subQ6=makeQuery(id+"F0.imprint","INTERSECT",VERTEX,{"derivedFrom":[subQ5,subQ0]});Q32=makeQuery(id+"F0.imprint","IMPRINT",FACE,{"disambiguationData":[TD([[makeQuery(id+"F0.imprint","IMPRINT",EDGE,{"disambiguationData":[TD([[subQ6,-1.0]])],"derivedFrom":subQ5}),-1.0]])]});}
            var Q33;
            {var subQ5=sQuery(id+"F0.wireOp",EDGE,"E56");Q33=makeQuery(id+"F0.imprint","IMPRINT",FACE,{"disambiguationData":[TD([[makeQuery(id+"F0.imprint","IMPRINT",EDGE,{"derivedFrom":subQ5}),1.0]])]});}
            var Q34;
            {var subQ0=sQuery(id+"F0.wireOp",EDGE,"E25");var subQ5=sQuery(id+"F0.wireOp",EDGE,"E2");var subQ6=makeQuery(id+"F0.imprint","INTERSECT",VERTEX,{"derivedFrom":[subQ5,subQ0]});Q34=makeQuery(id+"F0.imprint","IMPRINT",FACE,{"disambiguationData":[TD([[makeQuery(id+"F0.imprint","IMPRINT",EDGE,{"disambiguationData":[TD([[subQ6,-1.0]])],"derivedFrom":subQ5}),-1.0]])]});}
            var Q35;
            {var subQ0=sQuery(id+"F0.wireOp",EDGE,"E5");var subQ5=sQuery(id+"F0.wireOp",EDGE,"E2");var subQ6=makeQuery(id+"F0.imprint","INTERSECT",VERTEX,{"derivedFrom":[subQ5,subQ0]});Q35=makeQuery(id+"F0.imprint","IMPRINT",FACE,{"disambiguationData":[TD([[makeQuery(id+"F0.imprint","IMPRINT",EDGE,{"disambiguationData":[TD([[subQ6,-1.0]])],"derivedFrom":subQ5}),-1.0]])]});}
            var Q36;
            {var subQ5=sQuery(id+"F0.wireOp",EDGE,"E55");Q36=makeQuery(id+"F0.imprint","IMPRINT",FACE,{"disambiguationData":[TD([[makeQuery(id+"F0.imprint","IMPRINT",EDGE,{"derivedFrom":subQ5}),1.0]])]});}
            var Q37;
            {var subQ0=sQuery(id+"F0.wireOp",EDGE,"E3");var subQ5=sQuery(id+"F0.wireOp",EDGE,"E2");var subQ6=makeQuery(id+"F0.imprint","INTERSECT",VERTEX,{"derivedFrom":[subQ5,subQ0]});Q37=makeQuery(id+"F0.imprint","IMPRINT",FACE,{"disambiguationData":[TD([[makeQuery(id+"F0.imprint","IMPRINT",EDGE,{"disambiguationData":[TD([[subQ6,-1.0]])],"derivedFrom":subQ5}),-1.0]])]});}
            var Q38;
            {var subQ5=sQuery(id+"F0.wireOp",EDGE,"E54");Q38=makeQuery(id+"F0.imprint","IMPRINT",FACE,{"disambiguationData":[TD([[makeQuery(id+"F0.imprint","IMPRINT",EDGE,{"derivedFrom":subQ5}),1.0]])]});}
            var Q39;
            {var subQ5=sQuery(id+"F0.wireOp",EDGE,"E53");Q39=makeQuery(id+"F0.imprint","IMPRINT",FACE,{"disambiguationData":[TD([[makeQuery(id+"F0.imprint","IMPRINT",EDGE,{"derivedFrom":subQ5}),1.0]])]});}
            extrude(context, id + "F3", {"entities" : qUnion([Q0, Q1, Q2, Q3, Q4, Q5, Q6, Q7, Q8, Q9, Q10, Q11, Q12, Q13, Q14, Q15, Q16, Q17, Q18, Q19, Q20, Q21, Q22, Q23, Q24, Q25, Q26, Q27, Q28, Q29, Q30, Q31, Q32, Q33, Q34, Q35, Q36, Q37, Q38, Q39]), "oppositeDirection" : true, "depth" : 7.11 * mm});
        }
        {
            var Q0;
            {var subQ36=sQuery(id+"F0.wireOp",EDGE,"E67");Q0=makeQuery(id+"F0.imprint","IMPRINT",FACE,{"disambiguationData":[TD([[makeQuery(id+"F0.imprint","IMPRINT",EDGE,{"derivedFrom":subQ36}),-1.0]])]});}
            var Q1;
            {var subQ0=sQuery(id+"F0.wireOp",EDGE,"E43");var subQ1=sQuery(id+"F0.wireOp",EDGE,"E1");var subQ2=makeQuery(id+"F0.imprint","INTERSECT",VERTEX,{"derivedFrom":[subQ1,subQ0]});Q1=makeQuery(id+"F0.imprint","IMPRINT",FACE,{"disambiguationData":[TD([[makeQuery(id+"F0.imprint","IMPRINT",EDGE,{"disambiguationData":[TD([[subQ2,-1.0]])],"derivedFrom":subQ1}),1.0]])]});}
            var Q2;
            {var subQ0=sQuery(id+"F0.wireOp",EDGE,"E23");var subQ1=sQuery(id+"F0.wireOp",EDGE,"E1");var subQ2=makeQuery(id+"F0.imprint","INTERSECT",VERTEX,{"derivedFrom":[subQ1,subQ0]});Q2=makeQuery(id+"F0.imprint","IMPRINT",FACE,{"disambiguationData":[TD([[makeQuery(id+"F0.imprint","IMPRINT",EDGE,{"disambiguationData":[TD([[subQ2,-1.0]])],"derivedFrom":subQ1}),1.0]])]});}
            var Q3;
            {var subQ0=sQuery(id+"F0.wireOp",EDGE,"E21");var subQ1=sQuery(id+"F0.wireOp",EDGE,"E1");var subQ2=makeQuery(id+"F0.imprint","INTERSECT",VERTEX,{"derivedFrom":[subQ1,subQ0]});Q3=makeQuery(id+"F0.imprint","IMPRINT",FACE,{"disambiguationData":[TD([[makeQuery(id+"F0.imprint","IMPRINT",EDGE,{"disambiguationData":[TD([[subQ2,-1.0]])],"derivedFrom":subQ1}),1.0]])]});}
            var Q4;
            {var subQ0=sQuery(id+"F0.wireOp",EDGE,"E19");var subQ1=sQuery(id+"F0.wireOp",EDGE,"E1");var subQ2=makeQuery(id+"F0.imprint","INTERSECT",VERTEX,{"derivedFrom":[subQ1,subQ0]});Q4=makeQuery(id+"F0.imprint","IMPRINT",FACE,{"disambiguationData":[TD([[makeQuery(id+"F0.imprint","IMPRINT",EDGE,{"disambiguationData":[TD([[subQ2,-1.0]])],"derivedFrom":subQ1}),1.0]])]});}
            var Q5;
            {var subQ0=sQuery(id+"F0.wireOp",EDGE,"E17");var subQ1=sQuery(id+"F0.wireOp",EDGE,"E1");var subQ2=makeQuery(id+"F0.imprint","INTERSECT",VERTEX,{"derivedFrom":[subQ1,subQ0]});Q5=makeQuery(id+"F0.imprint","IMPRINT",FACE,{"disambiguationData":[TD([[makeQuery(id+"F0.imprint","IMPRINT",EDGE,{"disambiguationData":[TD([[subQ2,-1.0]])],"derivedFrom":subQ1}),1.0]])]});}
            var Q6;
            {var subQ0=sQuery(id+"F0.wireOp",EDGE,"E14");var subQ1=sQuery(id+"F0.wireOp",EDGE,"E1");var subQ2=makeQuery(id+"F0.imprint","INTERSECT",VERTEX,{"derivedFrom":[subQ1,subQ0]});Q6=makeQuery(id+"F0.imprint","IMPRINT",FACE,{"disambiguationData":[TD([[makeQuery(id+"F0.imprint","IMPRINT",EDGE,{"disambiguationData":[TD([[subQ2,-1.0]])],"derivedFrom":subQ1}),1.0]])]});}
            var Q7;
            {var subQ0=sQuery(id+"F0.wireOp",EDGE,"E11");var subQ1=sQuery(id+"F0.wireOp",EDGE,"E1");var subQ2=makeQuery(id+"F0.imprint","INTERSECT",VERTEX,{"derivedFrom":[subQ1,subQ0]});Q7=makeQuery(id+"F0.imprint","IMPRINT",FACE,{"disambiguationData":[TD([[makeQuery(id+"F0.imprint","IMPRINT",EDGE,{"disambiguationData":[TD([[subQ2,-1.0]])],"derivedFrom":subQ1}),1.0]])]});}
            var Q8;
            {var subQ0=sQuery(id+"F0.wireOp",EDGE,"E3");var subQ1=sQuery(id+"F0.wireOp",EDGE,"E1");var subQ2=makeQuery(id+"F0.imprint","INTERSECT",VERTEX,{"derivedFrom":[subQ1,subQ0]});Q8=makeQuery(id+"F0.imprint","IMPRINT",FACE,{"disambiguationData":[TD([[makeQuery(id+"F0.imprint","IMPRINT",EDGE,{"disambiguationData":[TD([[subQ2,-1.0]])],"derivedFrom":subQ1}),1.0]])]});}
            var Q9;
            {var subQ0=sQuery(id+"F0.wireOp",EDGE,"E8");var subQ1=sQuery(id+"F0.wireOp",EDGE,"E1");var subQ2=makeQuery(id+"F0.imprint","INTERSECT",VERTEX,{"derivedFrom":[subQ1,subQ0]});Q9=makeQuery(id+"F0.imprint","IMPRINT",FACE,{"disambiguationData":[TD([[makeQuery(id+"F0.imprint","IMPRINT",EDGE,{"disambiguationData":[TD([[subQ2,-1.0]])],"derivedFrom":subQ1}),1.0]])]});}
            var Q10;
            {var subQ0=sQuery(id+"F0.wireOp",EDGE,"E5");var subQ1=sQuery(id+"F0.wireOp",EDGE,"E1");var subQ2=makeQuery(id+"F0.imprint","INTERSECT",VERTEX,{"derivedFrom":[subQ1,subQ0]});Q10=makeQuery(id+"F0.imprint","IMPRINT",FACE,{"disambiguationData":[TD([[makeQuery(id+"F0.imprint","IMPRINT",EDGE,{"disambiguationData":[TD([[subQ2,-1.0]])],"derivedFrom":subQ1}),1.0]])]});}
            var Q11;
            {var subQ0=sQuery(id+"F0.wireOp",EDGE,"E25");var subQ1=sQuery(id+"F0.wireOp",EDGE,"E1");var subQ2=makeQuery(id+"F0.imprint","INTERSECT",VERTEX,{"derivedFrom":[subQ1,subQ0]});Q11=makeQuery(id+"F0.imprint","IMPRINT",FACE,{"disambiguationData":[TD([[makeQuery(id+"F0.imprint","IMPRINT",EDGE,{"disambiguationData":[TD([[subQ2,-1.0]])],"derivedFrom":subQ1}),1.0]])]});}
            var Q12;
            {var subQ0=sQuery(id+"F0.wireOp",EDGE,"E64");var subQ1=sQuery(id+"F0.wireOp",EDGE,"E1");var subQ2=makeQuery(id+"F0.imprint","INTERSECT",VERTEX,{"derivedFrom":[subQ1,subQ0]});Q12=makeQuery(id+"F0.imprint","IMPRINT",FACE,{"disambiguationData":[TD([[makeQuery(id+"F0.imprint","IMPRINT",EDGE,{"disambiguationData":[TD([[subQ2,1.0]])],"derivedFrom":subQ1}),1.0]])]});}
            var Q13;
            {var subQ0=sQuery(id+"F0.wireOp",EDGE,"E27");var subQ1=sQuery(id+"F0.wireOp",EDGE,"E1");var subQ2=makeQuery(id+"F0.imprint","INTERSECT",VERTEX,{"derivedFrom":[subQ1,subQ0]});Q13=makeQuery(id+"F0.imprint","IMPRINT",FACE,{"disambiguationData":[TD([[makeQuery(id+"F0.imprint","IMPRINT",EDGE,{"disambiguationData":[TD([[subQ2,-1.0]])],"derivedFrom":subQ1}),1.0]])]});}
            var Q14;
            {var subQ0=sQuery(id+"F0.wireOp",EDGE,"E29");var subQ1=sQuery(id+"F0.wireOp",EDGE,"E1");var subQ2=makeQuery(id+"F0.imprint","INTERSECT",VERTEX,{"derivedFrom":[subQ1,subQ0]});Q14=makeQuery(id+"F0.imprint","IMPRINT",FACE,{"disambiguationData":[TD([[makeQuery(id+"F0.imprint","IMPRINT",EDGE,{"disambiguationData":[TD([[subQ2,-1.0]])],"derivedFrom":subQ1}),1.0]])]});}
            var Q15;
            {var subQ0=sQuery(id+"F0.wireOp",EDGE,"E31");var subQ1=sQuery(id+"F0.wireOp",EDGE,"E1");var subQ2=makeQuery(id+"F0.imprint","INTERSECT",VERTEX,{"derivedFrom":[subQ1,subQ0]});Q15=makeQuery(id+"F0.imprint","IMPRINT",FACE,{"disambiguationData":[TD([[makeQuery(id+"F0.imprint","IMPRINT",EDGE,{"disambiguationData":[TD([[subQ2,-1.0]])],"derivedFrom":subQ1}),1.0]])]});}
            var Q16;
            {var subQ0=sQuery(id+"F0.wireOp",EDGE,"E35");var subQ1=sQuery(id+"F0.wireOp",EDGE,"E1");var subQ2=makeQuery(id+"F0.imprint","INTERSECT",VERTEX,{"derivedFrom":[subQ1,subQ0]});Q16=makeQuery(id+"F0.imprint","IMPRINT",FACE,{"disambiguationData":[TD([[makeQuery(id+"F0.imprint","IMPRINT",EDGE,{"disambiguationData":[TD([[subQ2,-1.0]])],"derivedFrom":subQ1}),1.0]])]});}
            var Q17;
            {var subQ0=sQuery(id+"F0.wireOp",EDGE,"E33");var subQ1=sQuery(id+"F0.wireOp",EDGE,"E1");var subQ2=makeQuery(id+"F0.imprint","INTERSECT",VERTEX,{"derivedFrom":[subQ1,subQ0]});Q17=makeQuery(id+"F0.imprint","IMPRINT",FACE,{"disambiguationData":[TD([[makeQuery(id+"F0.imprint","IMPRINT",EDGE,{"disambiguationData":[TD([[subQ2,-1.0]])],"derivedFrom":subQ1}),1.0]])]});}
            var Q18;
            {var subQ0=sQuery(id+"F0.wireOp",EDGE,"E39");var subQ1=sQuery(id+"F0.wireOp",EDGE,"E1");var subQ2=makeQuery(id+"F0.imprint","INTERSECT",VERTEX,{"derivedFrom":[subQ1,subQ0]});Q18=makeQuery(id+"F0.imprint","IMPRINT",FACE,{"disambiguationData":[TD([[makeQuery(id+"F0.imprint","IMPRINT",EDGE,{"disambiguationData":[TD([[subQ2,-1.0]])],"derivedFrom":subQ1}),1.0]])]});}
            var Q19;
            {var subQ0=sQuery(id+"F0.wireOp",EDGE,"E41");var subQ1=sQuery(id+"F0.wireOp",EDGE,"E1");var subQ2=makeQuery(id+"F0.imprint","INTERSECT",VERTEX,{"derivedFrom":[subQ1,subQ0]});Q19=makeQuery(id+"F0.imprint","IMPRINT",FACE,{"disambiguationData":[TD([[makeQuery(id+"F0.imprint","IMPRINT",EDGE,{"disambiguationData":[TD([[subQ2,-1.0]])],"derivedFrom":subQ1}),1.0]])]});}
            var Q20;
            {var subQ0=sQuery(id+"F0.wireOp",EDGE,"E37");var subQ1=sQuery(id+"F0.wireOp",EDGE,"E1");var subQ2=makeQuery(id+"F0.imprint","INTERSECT",VERTEX,{"derivedFrom":[subQ1,subQ0]});Q20=makeQuery(id+"F0.imprint","IMPRINT",FACE,{"disambiguationData":[TD([[makeQuery(id+"F0.imprint","IMPRINT",EDGE,{"disambiguationData":[TD([[subQ2,-1.0]])],"derivedFrom":subQ1}),1.0]])]});}
            var Q21;
            Q21=makeQuery(id+"F0.imprint","IMPRINT",FACE,{"disambiguationData":[TD([[makeQuery(id+"F0.imprint","IMPRINT",EDGE,{"derivedFrom":sQuery(id+"F0.wireOp",EDGE,"E68")}),1.0]])]});
            var Q22;
            Q22=makeQuery(id+"F0.imprint","IMPRINT",FACE,{"disambiguationData":[TD([[makeQuery(id+"F0.imprint","IMPRINT",EDGE,{"derivedFrom":sQuery(id+"F0.wireOp",EDGE,"E70")}),1.0]])]});
            var Q23;
            Q23=makeQuery(id+"F0.imprint","IMPRINT",FACE,{"disambiguationData":[TD([[makeQuery(id+"F0.imprint","IMPRINT",EDGE,{"derivedFrom":sQuery(id+"F0.wireOp",EDGE,"E71")}),1.0]])]});
            var Q24;
            Q24=makeQuery(id+"F0.imprint","IMPRINT",FACE,{"disambiguationData":[TD([[makeQuery(id+"F0.imprint","IMPRINT",EDGE,{"derivedFrom":sQuery(id+"F0.wireOp",EDGE,"E69")}),1.0]])]});
            var Q25;
            Q25=makeQuery(id+"F0.imprint","IMPRINT",FACE,{"disambiguationData":[TD([[makeQuery(id+"F0.imprint","IMPRINT",EDGE,{"derivedFrom":sQuery(id+"F0.wireOp",EDGE,"E67")}),1.0]])]});
            var Q26;
            {var subQ0=sQuery(id+"F0.wireOp",EDGE,"E66");var subQ4=makeQuery(id+"F0.imprint","INTERSECT",VERTEX,{"derivedFrom":[subQ0,sQuery(id+"F0.wireOp",EDGE,"E68")]});Q26=makeQuery(id+"F0.imprint","IMPRINT",FACE,{"disambiguationData":[TD([[makeQuery(id+"F0.imprint","IMPRINT",EDGE,{"disambiguationData":[TD([[subQ4,1.0]])],"derivedFrom":subQ0}),1.0]])]});}
            var Q27;
            Q27=sQuery(id+"F0.wireOp",EDGE,"E1");
            extrude(context, id + "F4", {"entities" : qUnion([Q0, Q1, Q2, Q3, Q4, Q5, Q6, Q7, Q8, Q9, Q10, Q11, Q12, Q13, Q14, Q15, Q16, Q17, Q18, Q19, Q20, Q21, Q22, Q23, Q24, Q25, Q26]), "surfaceEntities" : qUnion([Q27]), "oppositeDirection" : true, "depth" : 2.03 * mm});
        }
        {
            var Q0;
            Q0=makeQuery(id+"F1.opExtrude","CAP_FACE",FACE,{"disambiguationData":[OSD([sQuery(id+"F0.wireOp",EDGE,"E3"),sQuery(id+"F0.wireOp",EDGE,"E4"),sQuery(id+"F0.wireOp",EDGE,"E5"),sQuery(id+"F0.wireOp",EDGE,"E6"),sQuery(id+"F0.wireOp",EDGE,"E7"),sQuery(id+"F0.wireOp",EDGE,"E8"),sQuery(id+"F0.wireOp",EDGE,"E10"),sQuery(id+"F0.wireOp",EDGE,"E11"),sQuery(id+"F0.wireOp",EDGE,"E13"),sQuery(id+"F0.wireOp",EDGE,"E14"),sQuery(id+"F0.wireOp",EDGE,"E16"),sQuery(id+"F0.wireOp",EDGE,"E17"),sQuery(id+"F0.wireOp",EDGE,"E18"),sQuery(id+"F0.wireOp",EDGE,"E19"),sQuery(id+"F0.wireOp",EDGE,"E20"),sQuery(id+"F0.wireOp",EDGE,"E21"),sQuery(id+"F0.wireOp",EDGE,"E22"),sQuery(id+"F0.wireOp",EDGE,"E23"),sQuery(id+"F0.wireOp",EDGE,"E24"),sQuery(id+"F0.wireOp",EDGE,"E25"),sQuery(id+"F0.wireOp",EDGE,"E26"),sQuery(id+"F0.wireOp",EDGE,"E27"),sQuery(id+"F0.wireOp",EDGE,"E28"),sQuery(id+"F0.wireOp",EDGE,"E29"),sQuery(id+"F0.wireOp",EDGE,"E30"),sQuery(id+"F0.wireOp",EDGE,"E31"),sQuery(id+"F0.wireOp",EDGE,"E32"),sQuery(id+"F0.wireOp",EDGE,"E33"),sQuery(id+"F0.wireOp",EDGE,"E34"),sQuery(id+"F0.wireOp",EDGE,"E35"),sQuery(id+"F0.wireOp",EDGE,"E36"),sQuery(id+"F0.wireOp",EDGE,"E37"),sQuery(id+"F0.wireOp",EDGE,"E38"),sQuery(id+"F0.wireOp",EDGE,"E39"),sQuery(id+"F0.wireOp",EDGE,"E40"),sQuery(id+"F0.wireOp",EDGE,"E41"),sQuery(id+"F0.wireOp",EDGE,"E42"),sQuery(id+"F0.wireOp",EDGE,"E43"),sQuery(id+"F0.wireOp",EDGE,"E44"),sQuery(id+"F0.wireOp",EDGE,"E45"),sQuery(id+"F0.wireOp",EDGE,"E46"),sQuery(id+"F0.wireOp",EDGE,"E47"),sQuery(id+"F0.wireOp",EDGE,"E48"),sQuery(id+"F0.wireOp",EDGE,"E49"),sQuery(id+"F0.wireOp",EDGE,"E50"),sQuery(id+"F0.wireOp",EDGE,"E51"),sQuery(id+"F0.wireOp",EDGE,"E52"),sQuery(id+"F0.wireOp",EDGE,"E53"),sQuery(id+"F0.wireOp",EDGE,"E54"),sQuery(id+"F0.wireOp",EDGE,"E55"),sQuery(id+"F0.wireOp",EDGE,"E56"),sQuery(id+"F0.wireOp",EDGE,"E57"),sQuery(id+"F0.wireOp",EDGE,"E58"),sQuery(id+"F0.wireOp",EDGE,"E59"),sQuery(id+"F0.wireOp",EDGE,"E60"),sQuery(id+"F0.wireOp",EDGE,"E61"),sQuery(id+"F0.wireOp",EDGE,"E62"),sQuery(id+"F0.wireOp",EDGE,"E63"),sQuery(id+"F0.wireOp",EDGE,"E64"),sQuery(id+"F0.wireOp",EDGE,"E65"),sQuery(id+"F0.wireOp",EDGE,"E67"),sQuery(id+"F0.wireOp",EDGE,"E68"),sQuery(id+"F0.wireOp",EDGE,"E69"),sQuery(id+"F0.wireOp",EDGE,"E70"),sQuery(id+"F0.wireOp",EDGE,"E71")])],"isStart":false});
            extrude(context, id + "F5", {"entities" : qUnion([Q0]), "oppositeDirection" : true, "depth" : 1.52 * mm});
        }
    });
